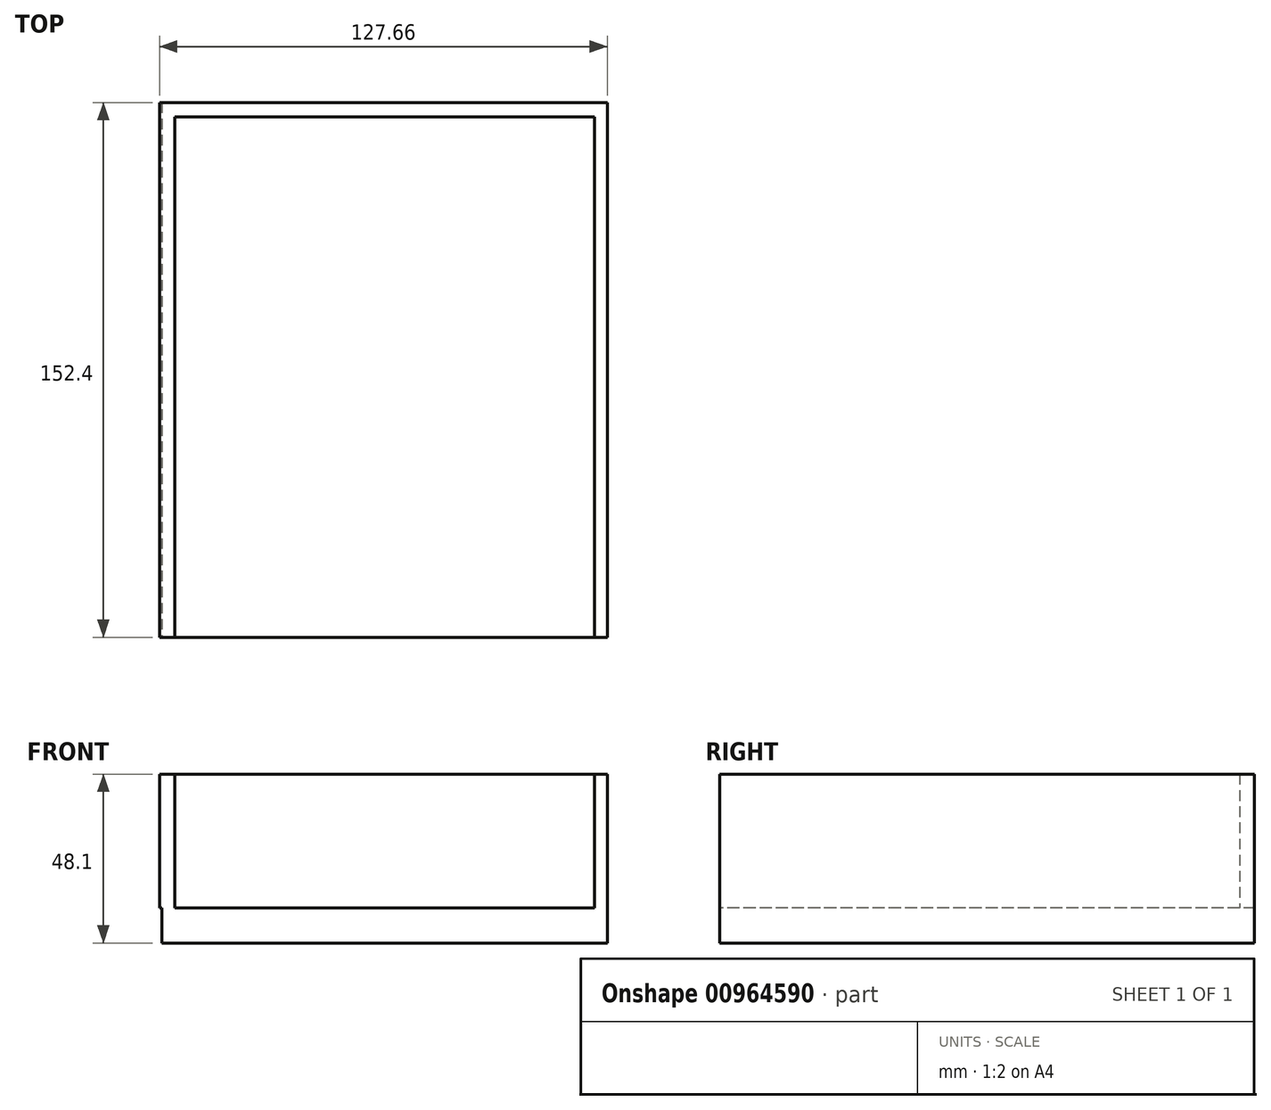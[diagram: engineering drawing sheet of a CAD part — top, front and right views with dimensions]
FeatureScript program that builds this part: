
annotation { "Feature Type Name" : "Feature", "Feature Type Description" : "" }
export const myFeature = defineFeature(function(context is Context, id is Id, definition is map)
    precondition{}
    {
        {
            var Q0;
            Q0=qCreatedBy(makeId("Top.planeOp"),FACE);
            var sketch = newSketch(context, id + "F0", { "sketchPlane" : qUnion([Q0])});
            skLineSegment(sketch, "E0.bottom", {"start": v(-62.69, 88.15) * mm, "end": v(64.31, 88.15) * mm});
            skLineSegment(sketch, "E0.top", {"start": v(-62.69, -64.25) * mm, "end": v(64.31, -64.25) * mm});
            skLineSegment(sketch, "E0.left", {"start": v(-62.69, 88.15) * mm, "end": v(-62.69, -64.25) * mm});
            skLineSegment(sketch, "E0.right", {"start": v(64.31, 88.15) * mm, "end": v(64.31, -64.25) * mm});
            skSolve(sketch);
        }
        {
            var Q0;
            Q0 = qSketchRegion(id + "F0", true);
            extrude(context, id + "F1", {"entities" : qUnion([Q0]), "depth" : 10 * mm, "offsetDistance" : 25.4 * mm});
        }
        {
            var Q0;
            Q0=makeQuery(id+"F1.opExtrude","CAP_FACE",FACE,{"disambiguationData":[OSD([sQuery(id+"F0.wireOp",EDGE,"E0.bottom"),sQuery(id+"F0.wireOp",EDGE,"E0.top"),sQuery(id+"F0.wireOp",EDGE,"E0.left"),sQuery(id+"F0.wireOp",EDGE,"E0.right")])],"isStart":false});
            var sketch = newSketch(context, id + "F2", { "sketchPlane" : qUnion([Q0])});
            skLineSegment(sketch, "E1.bottom", {"start": v(-63.35, 88.15) * mm, "end": v(-62.69, 88.15) * mm});
            skLineSegment(sketch, "E1.top", {"start": v(-63.35, -64.25) * mm, "end": v(-62.69, -64.25) * mm});
            skLineSegment(sketch, "E1.left", {"start": v(-62.69, 88.15) * mm, "end": v(-62.69, -64.25) * mm});
            skLineSegment(sketch, "E1.right", {"start": v(-63.35, 88.15) * mm, "end": v(-63.35, -64.25) * mm});
            skLineSegment(sketch, "E2.bottom", {"start": v(-63.35, 88.15) * mm, "end": v(64.31, 88.15) * mm});
            skLineSegment(sketch, "E2.top", {"start": v(-63.35, 88.15) * mm, "end": v(64.31, 88.15) * mm});
            skLineSegment(sketch, "E2.left", {"start": v(-63.35, 88.15) * mm, "end": v(-63.35, 88.15) * mm});
            skLineSegment(sketch, "E2.right", {"start": v(64.31, 88.15) * mm, "end": v(64.31, 88.15) * mm});
            skLineSegment(sketch, "E3.top", {"start": v(64.31, -64.25) * mm, "end": v(64.31, -64.25) * mm});
            skLineSegment(sketch, "E3.left", {"start": v(64.31, 88.15) * mm, "end": v(64.31, -64.25) * mm});
            skLineSegment(sketch, "E3.right", {"start": v(64.31, 88.15) * mm, "end": v(64.31, -64.25) * mm});
            skLineSegment(sketch, "E4.bottom", {"start": v(-62.69, 88.15) * mm, "end": v(-58.97, 88.15) * mm});
            skLineSegment(sketch, "E4.top", {"start": v(-62.69, -64.25) * mm, "end": v(-58.97, -64.25) * mm});
            skLineSegment(sketch, "E4.right", {"start": v(-58.97, 88.15) * mm, "end": v(-58.97, -64.25) * mm});
            skLineSegment(sketch, "E5.bottom", {"start": v(-58.97, 88.15) * mm, "end": v(64.31, 88.15) * mm});
            skLineSegment(sketch, "E5.top", {"start": v(-58.97, 84.02) * mm, "end": v(64.31, 84.02) * mm});
            skLineSegment(sketch, "E5.left", {"start": v(-58.97, 88.15) * mm, "end": v(-58.97, 84.02) * mm});
            skLineSegment(sketch, "E5.right", {"start": v(64.31, 88.15) * mm, "end": v(64.31, 84.02) * mm});
            skLineSegment(sketch, "E6.bottom", {"start": v(64.31, 84.02) * mm, "end": v(60.6, 84.02) * mm});
            skLineSegment(sketch, "E6.top", {"start": v(64.31, -64.25) * mm, "end": v(60.6, -64.25) * mm});
            skLineSegment(sketch, "E6.left", {"start": v(64.31, 84.02) * mm, "end": v(64.31, -64.25) * mm});
            skLineSegment(sketch, "E6.right", {"start": v(60.6, 84.02) * mm, "end": v(60.6, -64.25) * mm});
            skSolve(sketch);
        }
        {
            var Q0;
            Q0 = qSketchRegion(id + "F2", true);
            extrude(context, id + "F3", {"entities" : qUnion([Q0]), "operationType" : NewBodyOperationType.ADD, "depth" : 38.1 * mm, "offsetDistance" : 25.4 * mm});
        }
    });
